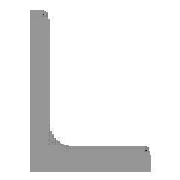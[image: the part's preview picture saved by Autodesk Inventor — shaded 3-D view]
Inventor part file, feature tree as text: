
AUTODESK INVENTOR PART (.ipt)
format: ipt  version: 2024.1 (Build 281209000, 209)  size: 120,832 bytes
history: native  units: mm (DEFAULTED — no unit token found)
features: other x4, sketch x1, plane x1
ambient origin geometry x8: Origin, YZ Plane, XZ Plane, XY Plane, X Axis, Y Axis, Z Axis, Center Point
bodies: Solid1 (feature_tree), Body (feature_tree)
feature tree (6):
  parser-record x1  (decoder bookkeeping rows leaked as tree rows — omitted from the tree; the rows remain in map.json)
  other  "Driven Length"
  other  "Start Plane"
  other  "End Plane"
  sketch  "Sketch3"  dims[d0=28.702mm d1=28.702mm d2=3.175mm d3=3.175mm d4=600.0mm d5=0.0mm d10=0.0mm d11=0.0mm d12=-0.0mm d13=600.0mm d14=2.286mm d15=1.27mm d16=90.0deg d17=600.0mm]
  plane  "Work Plane3"
